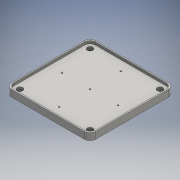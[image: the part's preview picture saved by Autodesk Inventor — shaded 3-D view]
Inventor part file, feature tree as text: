
AUTODESK INVENTOR PART (.ipt)
format: ipt  version: 2016 (Build 200138000, 138)  size: 172,544 bytes
history: native  units: mm
features: sketch x4, extrude x3, hole x1
ambient origin geometry x8: Origin, YZ Plane, XZ Plane, XY Plane, X Axis, Y Axis, Z Axis, Center Point
bodies: Body1 (feature_tree)
feature tree (8):
  extrude  "base"  Depth=150.0mm
  hole  "mountingHoles"  [1 undecoded]
  extrude  "spillTray"  Depth=7.5mm TaperAngle=0.0deg
  extrude  "Extrusion5"  Depth=2.0mm
  sketch  "Sketch5"  dims[d36=150.0mm d37=150.0mm]
  sketch  "Sketch6"  dims[d38=75.0mm d39=75.0mm]
  sketch  "Sketch7"  dims[d40=10.0mm d41=7.5mm d42=0.0mm]
  sketch  "Sketch9"  dims[d43=125.0mm d44=125.0mm d45=62.5mm d46=62.5mm d47=6.6mm d48=6.0mm d49=10.0mm d50=6.5mm d51=90.0deg d52=8.0mm d53=20.594885mm d54=2.0mm d55=2.0mm d56=2.0mm d57=2.0mm d58=10.0mm d59=10.0mm d60=10.0mm d61=10.0mm d62=5.0mm d63=0.0mm d73=2.65mm d74=2.65mm d75=2.65mm d76=2.65mm d77=2.65mm d78=55.0mm d79=55.0mm d80=50.0mm d81=50.0mm d82=2.0mm d83=0.0mm]
note: 1 required parameter value undecoded (feature->parameter linkage not recoverable at this tier; creation-order binding heuristic only, values carry confidence <= 0.55)
